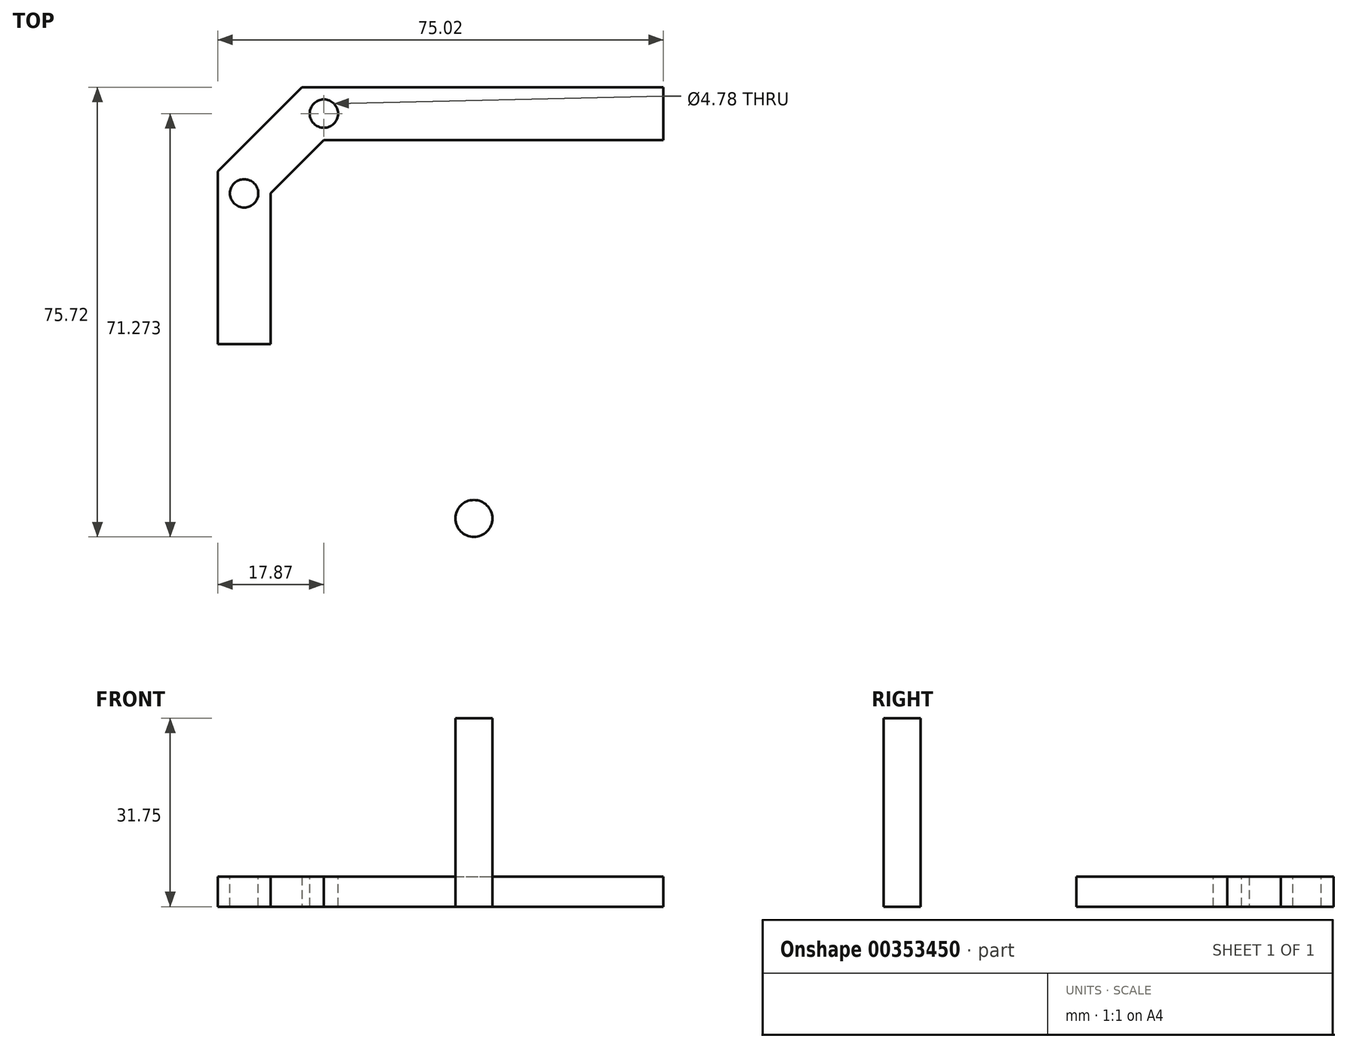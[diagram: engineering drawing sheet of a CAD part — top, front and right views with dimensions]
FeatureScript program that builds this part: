
annotation { "Feature Type Name" : "Feature", "Feature Type Description" : "" }
export const myFeature = defineFeature(function(context is Context, id is Id, definition is map)
    precondition{}
    {
        {
            var Q0;
            Q0=qCreatedBy(makeId("Top.planeOp"),FACE);
            var sketch = newSketch(context, id + "F0", { "sketchPlane" : qUnion([Q0])});
            skLineSegment(sketch, "E0.bottom", {"start": v(-15.69, 23.27) * mm, "end": v(41.46, 23.27) * mm});
            skLineSegment(sketch, "E0.top", {"start": v(-15.69, 14.38) * mm, "end": v(41.46, 14.38) * mm});
            skLineSegment(sketch, "E0.left", {"start": v(-15.69, 23.27) * mm, "end": v(-15.69, 14.38) * mm});
            skLineSegment(sketch, "E0.right", {"start": v(41.46, 23.27) * mm, "end": v(41.46, 14.38) * mm});
            skLineSegment(sketch, "E1", {"start": v(-15.69, 14.38) * mm, "end": v(-24.67, 5.4) * mm});
            skLineSegment(sketch, "E2.bottom", {"start": v(-24.67, 5.4) * mm, "end": v(-33.56, 5.4) * mm});
            skLineSegment(sketch, "E2.top", {"start": v(-24.67, -20) * mm, "end": v(-33.56, -20) * mm});
            skLineSegment(sketch, "E2.left", {"start": v(-24.67, 5.4) * mm, "end": v(-24.67, -20) * mm});
            skLineSegment(sketch, "E2.right", {"start": v(-33.56, 5.4) * mm, "end": v(-33.56, -20) * mm});
            skLineSegment(sketch, "E3", {"start": v(-20.18, 9.89) * mm, "end": v(-26.47, 16.17) * mm, "construction": true});
            skCircle(sketch, "E4", {"center": v(9.56, -49.34) * mm, "radius": 3.11 * mm});
            skLineSegment(sketch, "E5", {"start": v(-26.47, 16.17) * mm, "end": v(-19.37, 23.27) * mm});
            skLineSegment(sketch, "E6", {"start": v(-19.37, 23.27) * mm, "end": v(-33.56, 9.08) * mm});
            skLineSegment(sketch, "E7", {"start": v(-33.56, 9.08) * mm, "end": v(-33.56, 5.4) * mm});
            skLineSegment(sketch, "E8", {"start": v(-19.37, 23.27) * mm, "end": v(-15.69, 23.27) * mm});
            skSolve(sketch);
        }
        {
            var Q0;
            Q0=makeQuery(id+"F0.imprint","IMPRINT",FACE,{"disambiguationData":[TD([[makeQuery(id+"F0.imprint","IMPRINT",EDGE,{"derivedFrom":sQuery(id+"F0.wireOp",EDGE,"E0.bottom")}),-1.0]])]});
            var Q1;
            Q1=makeQuery(id+"F0.imprint","IMPRINT",FACE,{"disambiguationData":[TD([[makeQuery(id+"F0.imprint","IMPRINT",EDGE,{"derivedFrom":sQuery(id+"F0.wireOp",EDGE,"E2.bottom")}),1.0]])]});
            var Q2;
            Q2=makeQuery(id+"F0.imprint","IMPRINT",FACE,{"disambiguationData":[TD([[makeQuery(id+"F0.imprint","IMPRINT",EDGE,{"derivedFrom":sQuery(id+"F0.wireOp",EDGE,"E0.left")}),-1.0]])]});
            var Q3;
            Q3=makeQuery(id+"F0.imprint","IMPRINT",FACE,{"disambiguationData":[TD([[makeQuery(id+"F0.imprint","IMPRINT",EDGE,{"derivedFrom":sQuery(id+"F0.wireOp",EDGE,"E4")}),1.0]])]});
            extrude(context, id + "F1", {"entities" : qUnion([Q0, Q1, Q2, Q3]), "depth" : 5.08 * mm});
        }
        {
            var Q0;
            Q0=makeQuery(id+"F1.opExtrude","CAP_FACE",FACE,{"disambiguationData":[OSD([sQuery(id+"F0.wireOp",EDGE,"E0.bottom"),sQuery(id+"F0.wireOp",EDGE,"E0.top"),sQuery(id+"F0.wireOp",EDGE,"E0.right"),sQuery(id+"F0.wireOp",EDGE,"E1"),sQuery(id+"F0.wireOp",EDGE,"E2.top"),sQuery(id+"F0.wireOp",EDGE,"E2.left"),sQuery(id+"F0.wireOp",EDGE,"E2.right"),sQuery(id+"F0.wireOp",EDGE,"GqLAHHmt-vTlK-52TV-trtP-a6cZmRjWacH0"),sQuery(id+"F0.wireOp",EDGE,"kVDajMn9-F0pK-bnn1-J1GQ-mcezfiyIN3eN"),sQuery(id+"F0.wireOp",EDGE,"A38G81BY-DWhP-3dSV-6BC1-dlgzQ9pXKAkG")])],"isStart":false});
            var sketch = newSketch(context, id + "F2", { "sketchPlane" : qUnion([Q0])});
            skLineSegment(sketch, "E9", {"start": v(-15.69, 14.38) * mm, "end": v(-15.69, 23.27) * mm, "construction": true});
            skLineSegment(sketch, "E10", {"start": v(-24.67, 5.4) * mm, "end": v(-33.56, 5.4) * mm, "construction": true});
            skCircle(sketch, "E11", {"center": v(-15.69, 18.82) * mm, "radius": 2.39 * mm});
            skCircle(sketch, "E12", {"center": v(-29.11, 5.4) * mm, "radius": 2.38 * mm});
            skSolve(sketch);
        }
        {
            var Q0;
            Q0=makeQuery(id+"F2.imprint","IMPRINT",FACE,{"disambiguationData":[TD([[makeQuery(id+"F2.imprint","IMPRINT",EDGE,{"derivedFrom":sQuery(id+"F2.wireOp",EDGE,"E12")}),1.0]])]});
            var Q1;
            Q1=makeQuery(id+"F2.imprint","IMPRINT",FACE,{"disambiguationData":[TD([[makeQuery(id+"F2.imprint","IMPRINT",EDGE,{"derivedFrom":sQuery(id+"F2.wireOp",EDGE,"E11")}),1.0]])]});
            extrude(context, id + "F3", {"entities" : qUnion([Q0, Q1]), "operationType" : NewBodyOperationType.REMOVE, "endBound" : BoundingType.THROUGH_ALL, "oppositeDirection" : true, "depth" : 5.08 * mm});
        }
        {
            var Q0;
            Q0=makeQuery(id+"F1.opExtrude","CAP_FACE",FACE,{"disambiguationData":[OSD([sQuery(id+"F0.wireOp",EDGE,"E4")])],"isStart":false});
            extrude(context, id + "F4", {"entities" : qUnion([Q0]), "operationType" : NewBodyOperationType.ADD, "depth" : 26.67 * mm});
        }
    });
